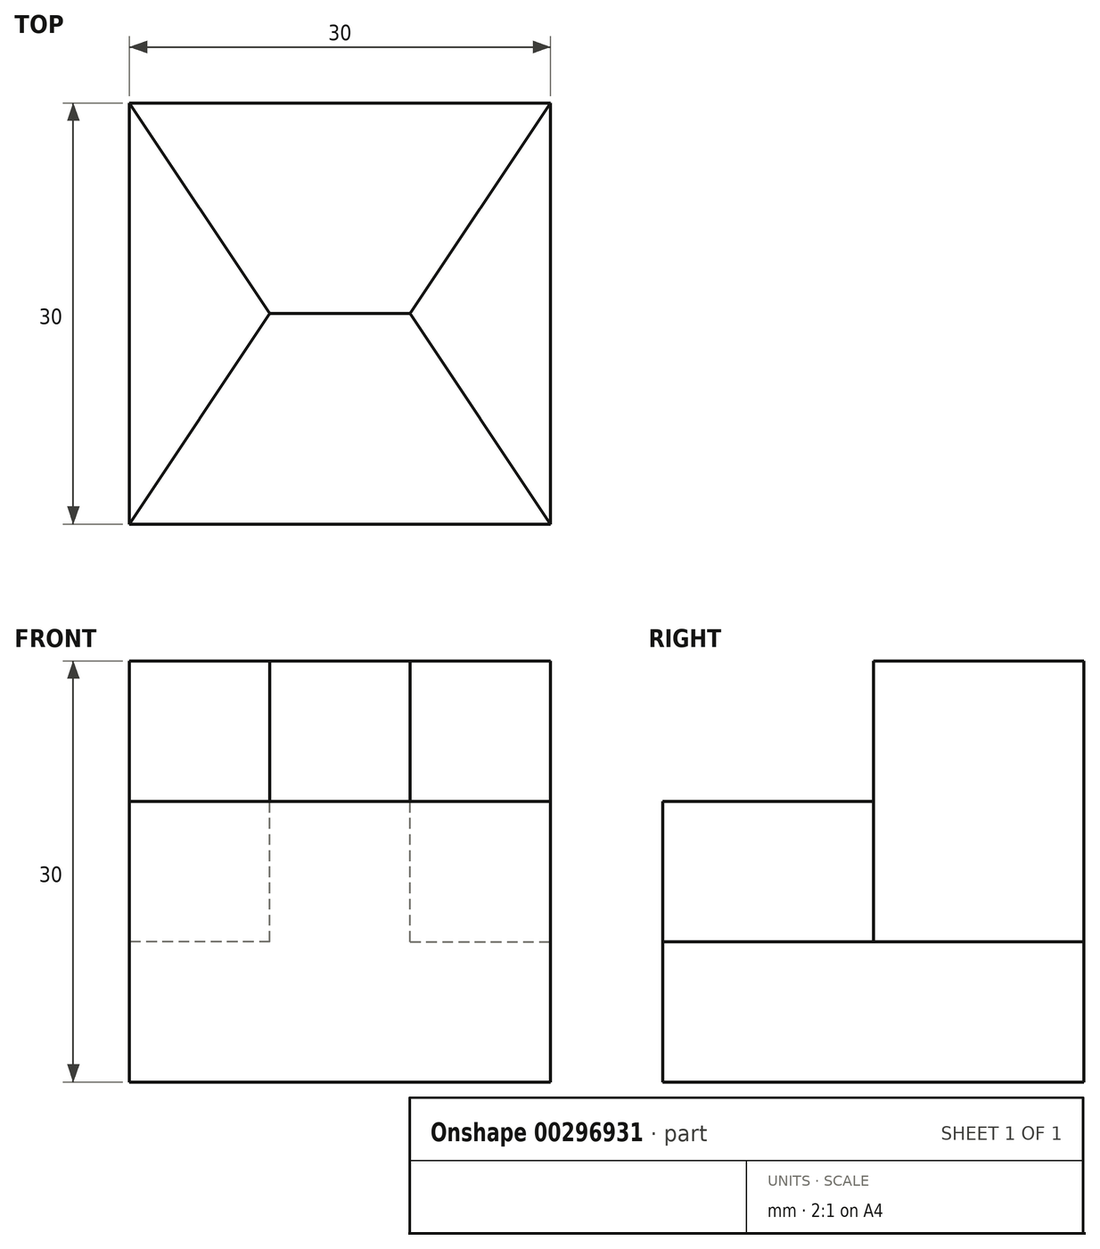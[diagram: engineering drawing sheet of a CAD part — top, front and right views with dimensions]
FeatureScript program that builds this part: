
annotation { "Feature Type Name" : "Feature", "Feature Type Description" : "" }
export const myFeature = defineFeature(function(context is Context, id is Id, definition is map)
    precondition{}
    {
        {
            var Q0;
            Q0=qCreatedBy(makeId("Top.planeOp"),FACE);
            var sketch = newSketch(context, id + "F0", { "sketchPlane" : qUnion([Q0])});
            skLineSegment(sketch, "E0.bottom", {"start": v(0, 0) * mm, "end": v(30, 0) * mm});
            skLineSegment(sketch, "E0.top", {"start": v(0, 30) * mm, "end": v(30, 30) * mm});
            skLineSegment(sketch, "E0.left", {"start": v(0, 0) * mm, "end": v(0, 30) * mm});
            skLineSegment(sketch, "E0.right", {"start": v(30, 0) * mm, "end": v(30, 30) * mm});
            skLineSegment(sketch, "E1", {"start": v(0, 30) * mm, "end": v(10, 15) * mm});
            skLineSegment(sketch, "E2", {"start": v(10, 15) * mm, "end": v(0, 0) * mm});
            skLineSegment(sketch, "E3", {"start": v(10, 15) * mm, "end": v(20, 15) * mm});
            skLineSegment(sketch, "E4", {"start": v(20, 15) * mm, "end": v(30, 30) * mm});
            skLineSegment(sketch, "E5", {"start": v(20, 15) * mm, "end": v(30, 0) * mm});
            skSolve(sketch);
        }
        {
            var Q0;
            Q0=qSketchRegion(id+"F0",true);
            extrude(context, id + "F1", {"entities" : qUnion([Q0]), "oppositeDirection" : true, "depth" : 30 * mm});
        }
        {
            var Q0;
            Q0=makeQuery(id+"F0.imprint","IMPRINT",FACE,{"disambiguationData":[TD([[makeQuery(id+"F0.imprint","IMPRINT",EDGE,{"derivedFrom":sQuery(id+"F0.wireOp",EDGE,"E0.bottom")}),1.0]])]});
            extrude(context, id + "F2", {"entities" : qUnion([Q0]), "operationType" : NewBodyOperationType.REMOVE, "oppositeDirection" : true, "depth" : 10 * mm});
        }
        {
            var Q0;
            Q0=makeQuery(id+"F0.imprint","IMPRINT",FACE,{"disambiguationData":[TD([[makeQuery(id+"F0.imprint","IMPRINT",EDGE,{"derivedFrom":sQuery(id+"F0.wireOp",EDGE,"E0.left")}),-1.0]])]});
            var Q1;
            Q1=makeQuery(id+"F0.imprint","IMPRINT",FACE,{"disambiguationData":[TD([[makeQuery(id+"F0.imprint","IMPRINT",EDGE,{"derivedFrom":sQuery(id+"F0.wireOp",EDGE,"E0.right")}),1.0]])]});
            extrude(context, id + "F3", {"entities" : qUnion([Q0, Q1]), "operationType" : NewBodyOperationType.REMOVE, "oppositeDirection" : true, "depth" : 20 * mm});
        }
    });
